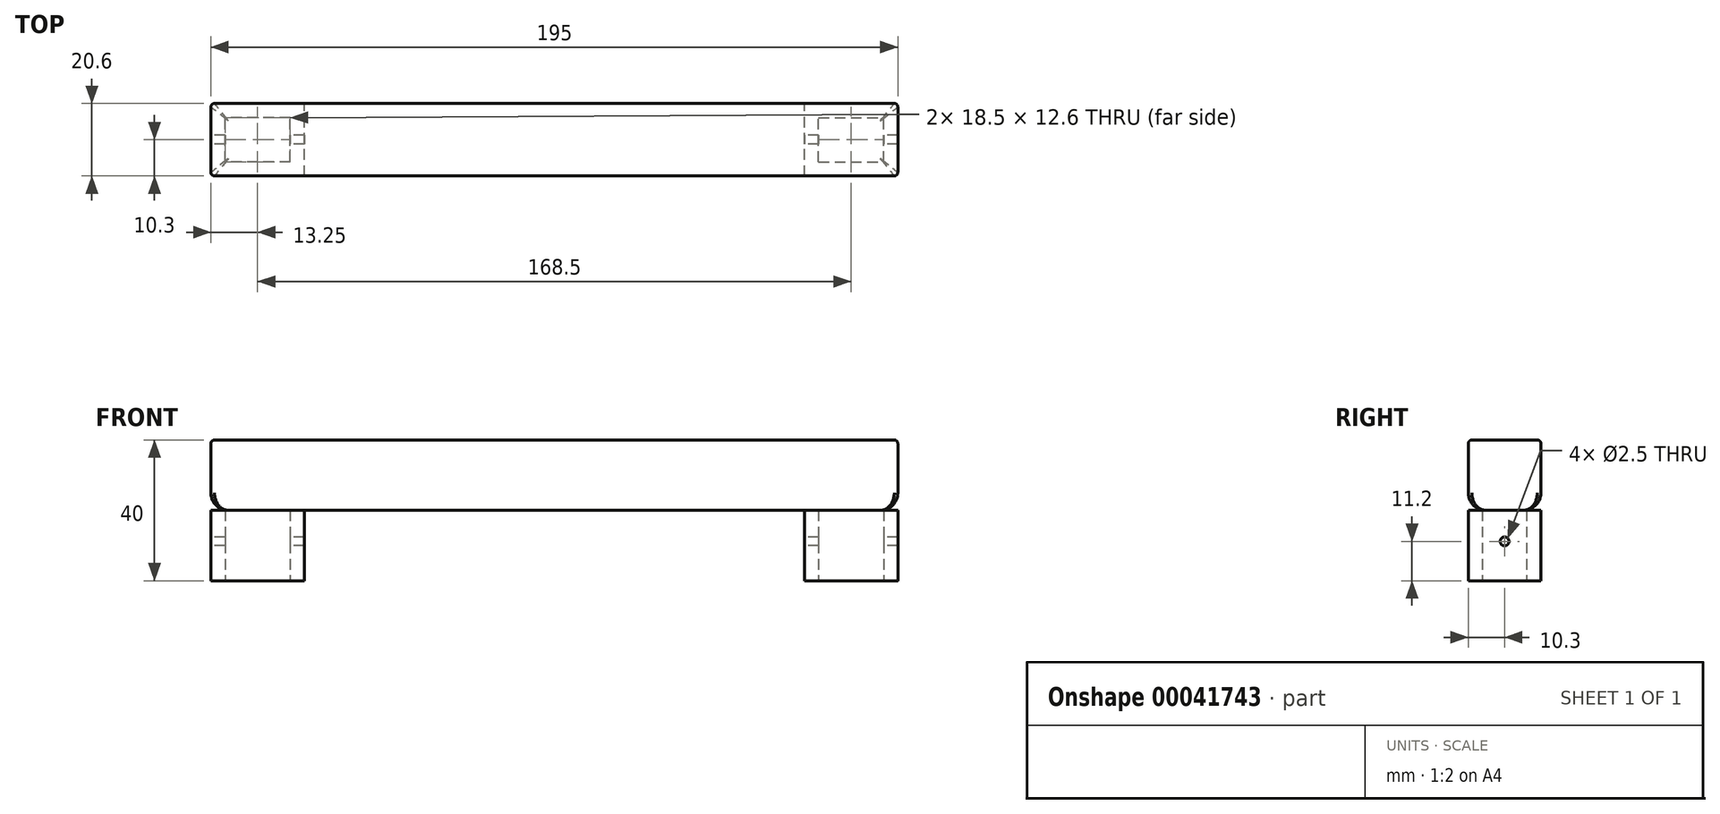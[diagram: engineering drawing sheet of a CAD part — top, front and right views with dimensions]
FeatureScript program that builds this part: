
annotation { "Feature Type Name" : "Feature", "Feature Type Description" : "" }
export const myFeature = defineFeature(function(context is Context, id is Id, definition is map)
    precondition{}
    {
        {
            var Q0;
            Q0=qCreatedBy(makeId("Top.planeOp"),FACE);
            var sketch = newSketch(context, id + "F0", { "sketchPlane" : qUnion([Q0])});
            skLineSegment(sketch, "E0.rect.bottom", {"start": v(-75, -6.3) * mm, "end": v(-93.5, -6.3) * mm});
            skLineSegment(sketch, "E0.rect.top", {"start": v(-75, 6.3) * mm, "end": v(-93.5, 6.3) * mm});
            skLineSegment(sketch, "E0.rect.left", {"start": v(-75, -6.3) * mm, "end": v(-75, 6.3) * mm});
            skLineSegment(sketch, "E0.rect.right", {"start": v(-93.5, -6.3) * mm, "end": v(-93.5, 6.3) * mm});
            skPoint(sketch, "E0.rect.middle", {"position": v(-84.25, 0) * mm});
            skLineSegment(sketch, "E1.rect.bottom", {"start": v(-71, -10.3) * mm, "end": v(-97.5, -10.3) * mm});
            skLineSegment(sketch, "E1.rect.top", {"start": v(-71, 10.3) * mm, "end": v(-97.5, 10.3) * mm});
            skLineSegment(sketch, "E1.rect.left", {"start": v(-71, -10.3) * mm, "end": v(-71, 10.3) * mm});
            skLineSegment(sketch, "E1.rect.right", {"start": v(-97.5, -10.3) * mm, "end": v(-97.5, 10.3) * mm});
            skLineSegment(sketch, "E2.MirrorCS", {"start": v(71, -10.3) * mm, "end": v(71, 10.3) * mm});
            skLineSegment(sketch, "E3.MirrorCS", {"start": v(71, 10.3) * mm, "end": v(97.5, 10.3) * mm});
            skLineSegment(sketch, "E4.MirrorCS", {"start": v(97.5, -10.3) * mm, "end": v(97.5, 10.3) * mm});
            skLineSegment(sketch, "E5.MirrorCS", {"start": v(71, -10.3) * mm, "end": v(97.5, -10.3) * mm});
            skLineSegment(sketch, "E6.MirrorCS", {"start": v(75, -6.3) * mm, "end": v(93.5, -6.3) * mm});
            skLineSegment(sketch, "E7.MirrorCS", {"start": v(75, -6.3) * mm, "end": v(75, 6.3) * mm});
            skLineSegment(sketch, "E8.MirrorCS", {"start": v(75, 6.3) * mm, "end": v(93.5, 6.3) * mm});
            skLineSegment(sketch, "E9.MirrorCS", {"start": v(93.5, -6.3) * mm, "end": v(93.5, 6.3) * mm});
            skSolve(sketch);
        }
        {
            var Q0;
            Q0 = qSketchRegion(id + "F0", true);
            extrude(context, id + "F1", {"entities" : qUnion([Q0]), "depth" : 20 * mm});
        }
        {
            var Q0;
            Q0=makeQuery(id+"F1.opExtrude","CAP_FACE",FACE,{"disambiguationData":[OSD([sQuery(id+"F0.wireOp",EDGE,"E0.rect.bottom"),sQuery(id+"F0.wireOp",EDGE,"E0.rect.top"),sQuery(id+"F0.wireOp",EDGE,"E0.rect.left"),sQuery(id+"F0.wireOp",EDGE,"E0.rect.right"),sQuery(id+"F0.wireOp",EDGE,"E1.rect.bottom"),sQuery(id+"F0.wireOp",EDGE,"E1.rect.top"),sQuery(id+"F0.wireOp",EDGE,"E1.rect.left"),sQuery(id+"F0.wireOp",EDGE,"E1.rect.right")])],"isStart":false});
            var sketch = newSketch(context, id + "F2", { "sketchPlane" : qUnion([Q0])});
            skLineSegment(sketch, "E10.bottom", {"start": v(-97.5, -10.3) * mm, "end": v(97.5, -10.3) * mm});
            skLineSegment(sketch, "E10.top", {"start": v(-97.5, 10.3) * mm, "end": v(97.5, 10.3) * mm});
            skLineSegment(sketch, "E10.left", {"start": v(-97.5, -10.3) * mm, "end": v(-97.5, 10.3) * mm});
            skLineSegment(sketch, "E10.right", {"start": v(97.5, -10.3) * mm, "end": v(97.5, 10.3) * mm});
            skSolve(sketch);
        }
        {
            var Q0;
            Q0 = qSketchRegion(id + "F2", true);
            extrude(context, id + "F3", {"entities" : qUnion([Q0]), "depth" : 20 * mm});
        }
        {
            var Q0;
            Q0=makeQuery(id+"F3.opExtrude","CAP_FACE",FACE,{"disambiguationData":[OSD([sQuery(id+"F2.wireOp",EDGE,"E10.bottom"),sQuery(id+"F2.wireOp",EDGE,"E10.top"),sQuery(id+"F2.wireOp",EDGE,"E10.left"),sQuery(id+"F2.wireOp",EDGE,"E10.right")])],"isStart":false});
            var Q1;
            Q1=makeQuery(id+"F3.opExtrude","SWEPT_EDGE",EDGE,{"disambiguationData":[OSD([sQuery(id+"F2.wireOp",EDGE,"E10.bottom"),sQuery(id+"F2.wireOp",EDGE,"E10.left")])]});
            var Q2;
            Q2=makeQuery(id+"F1.opExtrude","SWEPT_EDGE",EDGE,{"disambiguationData":[OSD([sQuery(id+"F0.wireOp",EDGE,"E1.rect.bottom"),sQuery(id+"F0.wireOp",EDGE,"E1.rect.right")])]});
            var Q3;
            Q3=makeQuery(id+"F3.opExtrude","SWEPT_EDGE",EDGE,{"disambiguationData":[OSD([sQuery(id+"F2.wireOp",EDGE,"E10.bottom"),sQuery(id+"F2.wireOp",EDGE,"E10.right")])]});
            var Q4;
            Q4=makeQuery(id+"F1.opExtrude","SWEPT_EDGE",EDGE,{"disambiguationData":[OSD([sQuery(id+"F0.wireOp",EDGE,"E4.MirrorCS"),sQuery(id+"F0.wireOp",EDGE,"E5.MirrorCS")])]});
            var Q5;
            Q5=makeQuery(id+"F1.opExtrude","SWEPT_EDGE",EDGE,{"disambiguationData":[OSD([sQuery(id+"F0.wireOp",EDGE,"E3.MirrorCS"),sQuery(id+"F0.wireOp",EDGE,"E4.MirrorCS")])]});
            var Q6;
            Q6=makeQuery(id+"F3.opExtrude","SWEPT_EDGE",EDGE,{"disambiguationData":[OSD([sQuery(id+"F2.wireOp",EDGE,"E10.top"),sQuery(id+"F2.wireOp",EDGE,"E10.right")])]});
            var Q7;
            Q7=makeQuery(id+"F1.opExtrude","SWEPT_EDGE",EDGE,{"disambiguationData":[OSD([sQuery(id+"F0.wireOp",EDGE,"E1.rect.top"),sQuery(id+"F0.wireOp",EDGE,"E1.rect.right")])]});
            var Q8;
            Q8=makeQuery(id+"F3.opExtrude","SWEPT_EDGE",EDGE,{"disambiguationData":[OSD([sQuery(id+"F2.wireOp",EDGE,"E10.top"),sQuery(id+"F2.wireOp",EDGE,"E10.left")])]});
            fillet(context, id + "F4", {"entities" : qUnion([Q0, Q1, Q2, Q3, Q4, Q5, Q6, Q7, Q8]), "radius" : 1 * mm, "tangentPropagation" : true, "allowEdgeOverflow" : false});
        }
        {
            var Q0;
            Q0=makeQuery(id+"F1.opExtrude","SWEPT_FACE",FACE,{"disambiguationData":[OSD([sQuery(id+"F0.wireOp",EDGE,"E1.rect.right")])]});
            var sketch = newSketch(context, id + "F5", { "sketchPlane" : qUnion([Q0])});
            skCircle(sketch, "E11", {"center": v(0, 11.2) * mm, "radius": 1.25 * mm});
            skSolve(sketch);
        }
        {
            var Q0;
            Q0 = qSketchRegion(id + "F5", true);
            extrude(context, id + "F6", {"entities" : qUnion([Q0]), "operationType" : NewBodyOperationType.REMOVE, "oppositeDirection" : true, "depth" : 2000 * mm});
        }
        {
            var Q0;
            Q0=makeQuery(id+"F1.opExtrude","SWEPT_FACE",FACE,{"disambiguationData":[OSD([sQuery(id+"F0.wireOp",EDGE,"E4.MirrorCS")])]});
            var sketch = newSketch(context, id + "F7", { "sketchPlane" : qUnion([Q0])});
            skCircle(sketch, "E12", {"center": v(0, 11.2) * mm, "radius": 1.25 * mm});
            skSolve(sketch);
        }
        {
            var Q0;
            Q0 = qSketchRegion(id + "F7", true);
            extrude(context, id + "F8", {"entities" : qUnion([Q0]), "operationType" : NewBodyOperationType.REMOVE, "oppositeDirection" : true, "depth" : 100 * mm});
        }
        {
            var Q0;
            Q0=makeQuery(id+"F3.opExtrude","CAP_EDGE",EDGE,{"disambiguationData":[OSD([sQuery(id+"F2.wireOp",EDGE,"E10.top")])],"isStart":true});
            var Q1;
            Q1=makeQuery(id+"F3.opExtrude","CAP_EDGE",EDGE,{"disambiguationData":[OSD([sQuery(id+"F2.wireOp",EDGE,"E10.bottom")])],"isStart":true});
            fillet(context, id + "F9", {"entities" : qUnion([Q0, Q1]), "radius" : 5 * mm, "tangentPropagation" : true, "allowEdgeOverflow" : false});
        }
    });
